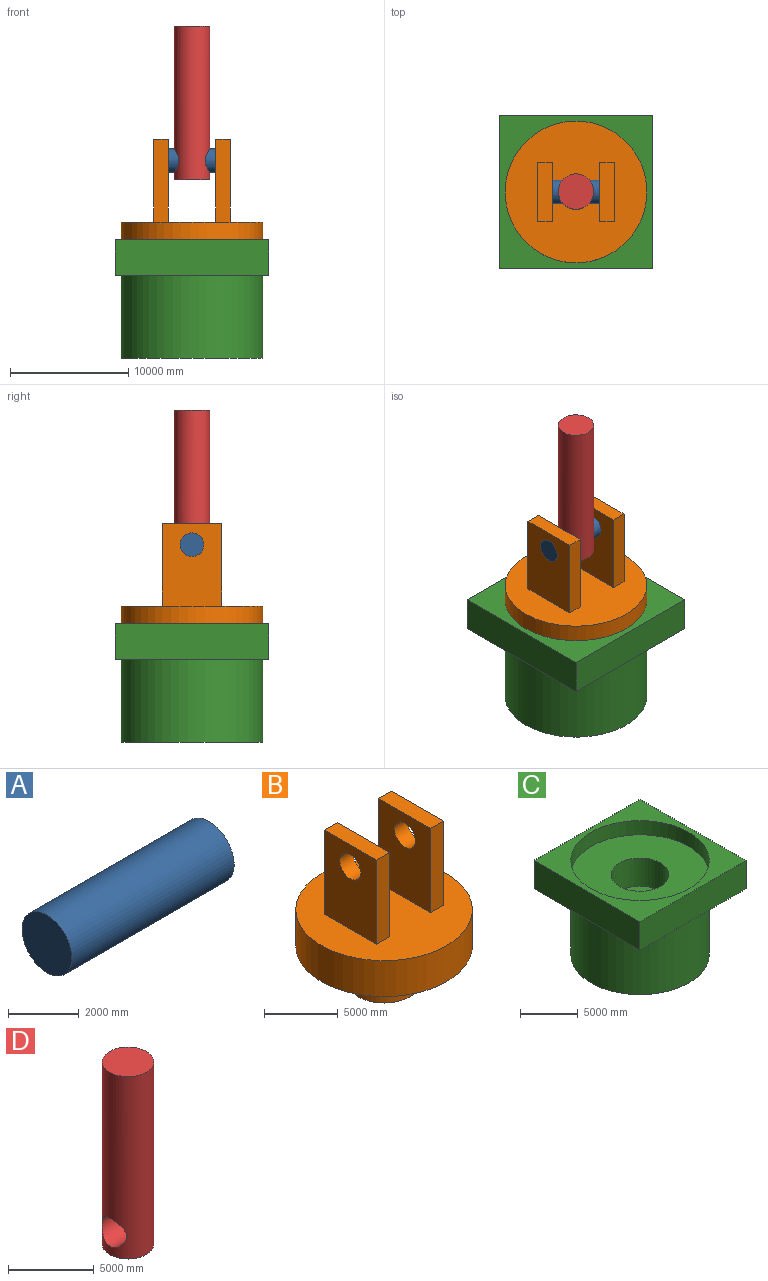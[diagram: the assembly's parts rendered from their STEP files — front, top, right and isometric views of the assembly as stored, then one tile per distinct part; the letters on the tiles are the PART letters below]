
ASSEMBLY  parts=4 mates=3
PART A: 3 faces, bbox 6500x2000x2000 mm
  f0: plane 2000x2000mm, normal (-1,0,0), area 3141592.7mm2, adj f1
  f1: cylinder r=1000mm len=6500mm, axis (1,0,0), area 40840704.5mm2, adj f0,f2
  f2: plane 2000x2000mm, normal (1,0,0), area 3141592.7mm2, adj f1
PART B: 17 faces, bbox 12000x12000x13000 mm
  f0: plane 12000x12000mm, normal (0,0,1), area 100597335.5mm2, adj f1,f3,f4,f5,f6,f8,f9,f10
  f1: cylinder r=6000mm len=12000mm, axis (0,0,-1), area 113097335.5mm2, adj f0,f2
  f2: plane 12000x12000mm, normal (0,0,-1), area 93462381.4mm2, adj f1,f13
  f3: plane 7000x5000mm, normal (-1,0,0), area 31858407.3mm2, adj f0,f4,f6,f7,f16
  f4: plane 7000x1250mm, normal (0,-1,0), area 8750000mm2, adj f0,f3,f5,f7
  f5: plane 7000x5000mm, normal (1,0,0), area 31858407.3mm2, adj f0,f4,f6,f7,f16
  f6: plane 7000x1250mm, normal (0,1,0), area 8750000mm2, adj f0,f3,f5,f7
  f7: plane 5000x1250mm, normal (0,0,1), area 6250000mm2, adj f3,f4,f5,f6
  f8: plane 7000x1250mm, normal (0,1,0), area 8750000mm2, adj f0,f9,f11,f12
  f9: plane 7000x5000mm, normal (-1,0,0), area 31858407.3mm2, adj f0,f8,f10,f12,f15
  f10: plane 7000x1250mm, normal (0,-1,0), area 8750000mm2, adj f0,f9,f11,f12
  f11: plane 7000x5000mm, normal (1,0,0), area 31858407.3mm2, adj f0,f8,f10,f12,f15
  f12: plane 5000x1250mm, normal (0,0,1), area 6250000mm2, adj f8,f9,f10,f11
  f13: cylinder r=2500mm len=5000mm, axis (0,0,1), area 47123889.8mm2, adj f2,f14
  f14: plane 5000x5000mm, normal (0,0,-1), area 19634954.1mm2, adj f13
  f15: cylinder r=1000mm len=2000mm, axis (1,0,0), area 7853981.6mm2, adj f9,f11
  f16: cylinder r=1000mm len=2000mm, axis (1,0,0), area 7853981.6mm2, adj f3,f5
PART C: 12 faces, bbox 13000x13000x10000 mm
  f0: plane 13000x3000mm, normal (1,0,0), area 39000000mm2, adj f1,f3,f4,f5
  f1: plane 13000x3000mm, normal (0,1,0), area 39000000mm2, adj f0,f2,f4,f5
  f2: plane 13000x3000mm, normal (-1,0,0), area 39000000mm2, adj f1,f3,f4,f5
  f3: plane 13000x3000mm, normal (0,-1,0), area 39000000mm2, adj f0,f2,f4,f5
  f4: plane 13000x13000mm, normal (0,0,1), area 55902664.5mm2, adj f0,f1,f2,f3,f8
  f5: plane 13000x13000mm, normal (0,0,-1), area 55902664.5mm2, adj f0,f1,f2,f3,f6
  f6: cylinder r=6000mm len=12000mm, axis (0,0,1), area 263893782.9mm2, adj f5,f7
  f7: plane 12000x12000mm, normal (0,0,-1), area 113097335.5mm2, adj f6
  f8: cylinder r=6000mm len=12000mm, axis (0,0,-1), area 56548667.8mm2, adj f4,f9
  f9: plane 12000x12000mm, normal (0,0,1), area 93462381.4mm2, adj f8,f10
  f10: cylinder r=2500mm len=5000mm, axis (0,0,1), area 47123889.8mm2, adj f9,f11
  f11: plane 5000x5000mm, normal (0,0,1), area 19634954.1mm2, adj f10
PART D: 4 faces, bbox 3000x3000x13000 mm
  f0: cylinder r=1500mm len=13000mm, axis (0,0,-1), area 115818236.3mm2, adj f1,f2,f3
  f1: plane 3000x3000mm, normal (0,0,1), area 7068583.5mm2, adj f0
  f2: plane 3000x3000mm, normal (0,0,-1), area 7068583.5mm2, adj f0
  f3: cylinder r=1000mm len=3000.01mm, axis (1,0,0), area 16535127.7mm2, adj f0
PLACE A at identity
PLACE B at identity
PLACE C at identity fixed
PLACE D rot(axis=(-0.13,-0.84,-0.53),0deg) t=(-0.08,0,0)mm
MATE revolute B.f1 <-> C.f6  axis (0,0,-1) through (0,0,-1500)mm
MATE fastened D.f3 <-> A.f1  axis (1,0,0) through (0,0,9700)mm
MATE revolute A.f1 <-> B.f15  axis (1,0,0) through (3250,0,9700)mm
